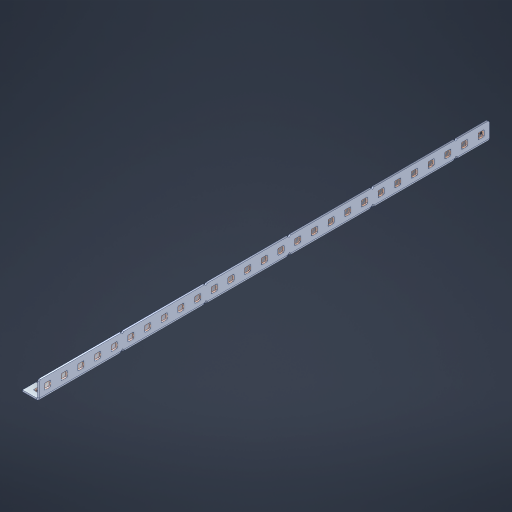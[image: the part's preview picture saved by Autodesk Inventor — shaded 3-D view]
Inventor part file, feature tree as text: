
AUTODESK INVENTOR PART (.ipt)
format: ipt  version: 2023 (Build 270158000, 158)  size: 1,135,104 bytes
history: native  units: in
note: dims shown in document units (in); Inventor stores cm internally (conversion verified against a paired STEP export)
features: other x88, extrude x79, sheet_metal_op x11, sketch x10, pattern_linear x2, mirror x1, chamfer x1
ambient origin geometry x8: Origin, YZ Plane, XZ Plane, XY Plane, X Axis, Y Axis, Z Axis, Center Point
bodies: Solid1 (feature_tree), Body (feature_tree)
feature tree (192):
  sheet_metal_op  "Flanges"
  other  "Flange Pattern Plane"
  other  "Flange Pattern Sketch"
  sheet_metal_op  "Flange Pattern"
  sheet_metal_op  "Body Pattern"
  pattern_linear  "Center Pattern"  Spacing1=0.0469in  [1 undecoded]
  other  "Arc Length"
  mirror  "Notch Mirror"
  pattern_linear  "Notch Pattern"  Spacing1=0.182in  [1 undecoded]
  chamfer  "End Chamfer"
  extrude  "Half Cut"  Depth=0.02in
  sketch  "Sketch1"  dims[d0=1.0in]
  other  "Plate1"
  sketch  "Sketch2"  dims[d1=13.5in]
  other  "Plate2"
  sheet_metal_op  "Bend1"
  sheet_metal_op  "Corner1"
  sketch  "Sketch3"  dims[d2=0.0469in]
  sketch  "Sketch7"  dims[d3=0.0469in]
  other  "Srf1"
  other  "Srf2"
  sketch  "Sketch8"  dims[d4=0.0234in]
  sketch  "Sketch9"  dims[d5=0.0938in]
  other  "Srf91"
  sheet_metal_op  "Body Pattern Sketch"
  other  "Srf92"
  sketch  "Sketch13"  dims[d6=0.0469in]
  sketch  "Sketch14"  dims[d7=0.5in d8=90.0deg d9=0.0312in]
  sketch  "Sketch15"  dims[d10=0.1875in]
  sketch  "Sketch16"  dims[d11=0.0469in d12=0.0469in d16=0.182in d17=0.02in d18=0.0469in d19=0.0in d20=0.25in d21=0.25in d38=10.6299in d40=0.5in d41=0.3937in d43=1.0in d46=0.172in d47=1.0in d48=0.0in d49=0.182in d50=0.02in d51=0.25in d52=0.25in d53=0.0469in d54=0.0in d55=0.172in d56=1.0in d57=0.0in d58=0.25in d60=10.6299in d62=0.5in d63=0.3937in d65=0.5in d85=0.1227in d86=0.1659in d88=0.04in d89=0.0469in d90=0.0in d91=0.04in d92=0.0491in d95=2.5in d96=0.04in d97=0.25in d98=45.0deg d99=0.25in d100=0.5in d101=0.0in d102=2.497in d106=0.182in d107=0.02in d108=0.5in d109=0.5in d110=0.0469in d111=0.0in d112=0.172in d113=0.5in d114=0.0in d117=0.5in d118=0.5in d119=0.5in]
  other  "Srf786"
  other  "Srf823"
  other  "Srf824"
  other  "Srf825"
  other  "Srf826"
  other  "Srf827"
  other  "Srf828"
  other  "Srf829"
  other  "Srf856"
  other  "Srf857"
  other  "Srf858"
  other  "Srf859"
  other  "Srf860"
  other  "Srf861"
  other  "Srf862"
  other  "Srf889"
  other  "Srf890"
  other  "Srf891"
  other  "Srf892"
  other  "Srf893"
  other  "Srf894"
  other  "Srf895"
  other  "Srf896"
  other  "Srf922"
  other  "Srf923"
  other  "Srf924"
  other  "Srf925"
  other  "Srf926"
  other  "Srf959"
  other  "Srf960"
  other  "Srf961"
  other  "Srf962"
  other  "Srf963"
  other  "Srf996"
  other  "Srf997"
  other  "Srf998"
  other  "Srf999"
  other  "Srf1000"
  other  "Srf1143"
  other  "Srf1144"
  other  "Srf1145"
  other  "Srf1146"
  other  "Srf1147"
  other  "Srf1148"
  other  "Srf1149"
  other  "Srf1150"
  other  "Srf1151"
  other  "Srf1152"
  other  "Srf1153"
  other  "Srf1154"
  other  "Srf1155"
  other  "Srf1199"
  other  "Srf1200"
  other  "Srf1201"
  other  "Srf1202"
  other  "Srf1203"
  other  "Srf1204"
  other  "Srf1205"
  other  "Srf1206"
  other  "Srf1207"
  other  "Srf1208"
  other  "Srf1209"
  other  "Srf1210"
  other  "Srf1211"
  other  "Srf1255"
  other  "Srf1256"
  other  "Srf1257"
  other  "Srf1258"
  other  "Srf1259"
  other  "Srf1260"
  other  "Srf1261"
  other  "Srf1262"
  other  "Srf1263"
  other  "Srf1264"
  other  "Srf1265"
  other  "Srf1266"
  other  "Srf1267"
  sheet_metal_op  "Flange Stamp"
  sheet_metal_op  "Flange Circle"
  sheet_metal_op  "Body Stamp"
  sheet_metal_op  "Body Circle"
  other  "Center Stamp"
  other  "Center Circle"
  sheet_metal_op  "Notch"
  extrude  "ExtrusionSrf2"  Depth=0.0469in
  extrude  "ExtrusionSrf92"  TaperAngle=0.0deg  [1 undecoded]
  extrude  "ExtrusionSrf823"  Depth=0.5in
  extrude  "ExtrusionSrf824"  Depth=0.5in
  extrude  "ExtrusionSrf825"  Depth=0.5in
  extrude  "ExtrusionSrf826"  Depth=0.5in
  extrude  "ExtrusionSrf827"  Depth=1.0in TaperAngle=0.0deg
  extrude  "ExtrusionSrf828"  Depth=0.182in
  extrude  "ExtrusionSrf829"  Depth=0.02in
  extrude  "ExtrusionSrf856"  Depth=0.5in
  extrude  "ExtrusionSrf857"  Depth=0.5in
  extrude  "ExtrusionSrf858"  Depth=0.0469in
  extrude  "ExtrusionSrf859"  TaperAngle=0.0deg  [1 undecoded]
  extrude  "ExtrusionSrf860"  Depth=0.5in
  extrude  "ExtrusionSrf861"  Depth=1.0in TaperAngle=0.0deg
  extrude  "ExtrusionSrf862"  Depth=0.5in
  extrude  "ExtrusionSrf889"  Depth=0.5in
  extrude  "ExtrusionSrf890"  Depth=0.5in
  extrude  "ExtrusionSrf891"  Depth=0.5in
  extrude  "ExtrusionSrf892"  Depth=0.5in
  extrude  "ExtrusionSrf893"  Depth=0.5in
  extrude  "ExtrusionSrf894"  Depth=0.0469in
  extrude  "ExtrusionSrf895"  TaperAngle=0.0deg  [1 undecoded]
  extrude  "ExtrusionSrf896"  Depth=0.5in
  extrude  "ExtrusionSrf922"  Depth=0.5in
  extrude  "ExtrusionSrf923"  Depth=0.5in
  extrude  "ExtrusionSrf924"  Depth=0.5in TaperAngle=45.0deg
  extrude  "ExtrusionSrf925"  Depth=0.5in
  extrude  "ExtrusionSrf926"  Depth=0.5in TaperAngle=0.0deg
  extrude  "ExtrusionSrf959"  Depth=0.5in
  extrude  "ExtrusionSrf960"  Depth=0.182in
  extrude  "ExtrusionSrf961"  Depth=0.02in
  extrude  "ExtrusionSrf962"  Depth=0.5in
  extrude  "ExtrusionSrf963"  Depth=0.5in
  extrude  "ExtrusionSrf996"  Depth=0.0469in
  extrude  "ExtrusionSrf997"  TaperAngle=0.0deg  [1 undecoded]
  extrude  "ExtrusionSrf998"  Depth=0.5in
  extrude  "ExtrusionSrf999"  Depth=0.5in TaperAngle=0.0deg
  extrude  "ExtrusionSrf1000"  Depth=0.5in
  extrude  "ExtrusionSrf1143"  Depth=0.5in
  extrude  "ExtrusionSrf1144"  Depth=0.5in
  extrude  "ExtrusionSrf1145"  [1 undecoded]
  extrude  "ExtrusionSrf1146"  [1 undecoded]
  extrude  "ExtrusionSrf1147"  [1 undecoded]
  extrude  "ExtrusionSrf1148"  [1 undecoded]
  extrude  "ExtrusionSrf1149"  [1 undecoded]
  extrude  "ExtrusionSrf1150"  [1 undecoded]
  extrude  "ExtrusionSrf1151"  [1 undecoded]
  extrude  "ExtrusionSrf1152"  [1 undecoded]
  extrude  "ExtrusionSrf1153"  [1 undecoded]
  extrude  "ExtrusionSrf1154"  [1 undecoded]
  extrude  "ExtrusionSrf1155"  [1 undecoded]
  extrude  "ExtrusionSrf1199"  [1 undecoded]
  extrude  "ExtrusionSrf1200"  [1 undecoded]
  extrude  "ExtrusionSrf1201"  [1 undecoded]
  extrude  "ExtrusionSrf1202"  [1 undecoded]
  extrude  "ExtrusionSrf1203"  [1 undecoded]
  extrude  "ExtrusionSrf1204"  [1 undecoded]
  extrude  "ExtrusionSrf1205"  [1 undecoded]
  extrude  "ExtrusionSrf1206"  [1 undecoded]
  extrude  "ExtrusionSrf1207"  [1 undecoded]
  extrude  "ExtrusionSrf1208"  [1 undecoded]
  extrude  "ExtrusionSrf1209"  [1 undecoded]
  extrude  "ExtrusionSrf1210"  [1 undecoded]
  extrude  "ExtrusionSrf1211"  [1 undecoded]
  extrude  "ExtrusionSrf1255"  [1 undecoded]
  extrude  "ExtrusionSrf1256"  [1 undecoded]
  extrude  "ExtrusionSrf1257"  [1 undecoded]
  extrude  "ExtrusionSrf1258"  [1 undecoded]
  extrude  "ExtrusionSrf1259"  [1 undecoded]
  extrude  "ExtrusionSrf1260"  [1 undecoded]
  extrude  "ExtrusionSrf1261"  [1 undecoded]
  extrude  "ExtrusionSrf1262"  [1 undecoded]
  extrude  "ExtrusionSrf1263"  [1 undecoded]
  extrude  "ExtrusionSrf1264"  [1 undecoded]
  extrude  "ExtrusionSrf1265"  [1 undecoded]
  extrude  "ExtrusionSrf1266"  [1 undecoded]
  extrude  "ExtrusionSrf1267"  [1 undecoded]
note: 43 required parameter values undecoded (feature->parameter linkage not recoverable at this tier; creation-order binding heuristic only, values carry confidence <= 0.55)
